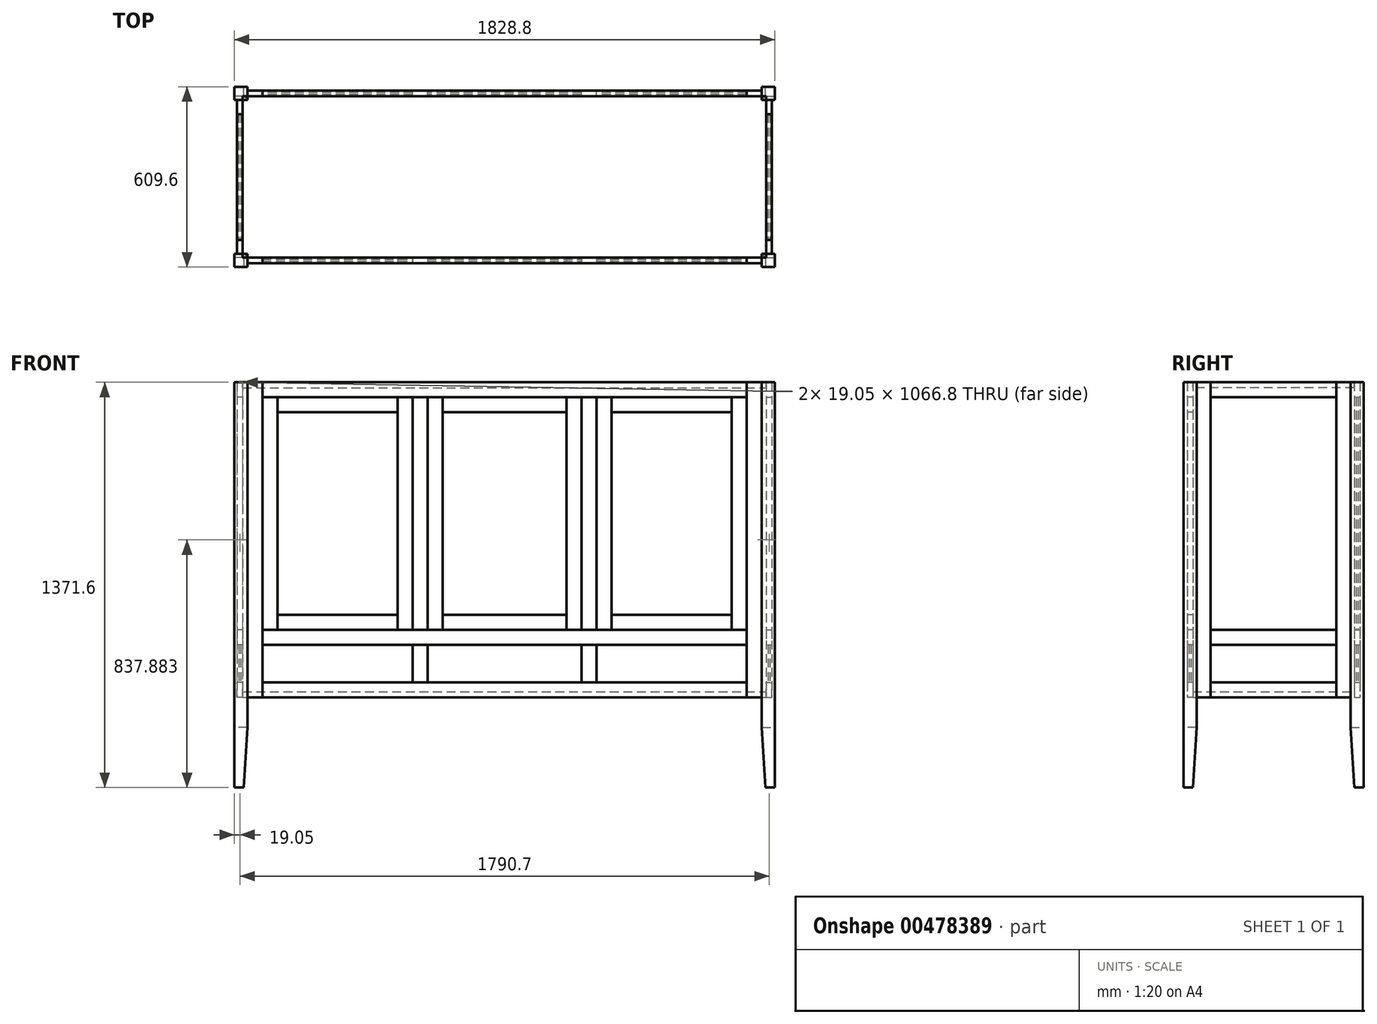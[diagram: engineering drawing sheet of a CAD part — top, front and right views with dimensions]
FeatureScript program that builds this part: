
annotation { "Feature Type Name" : "Feature", "Feature Type Description" : "" }
export const myFeature = defineFeature(function(context is Context, id is Id, definition is map)
    precondition{}
    {
        {
            var Q0;
            Q0=qCreatedBy(makeId("Front.planeOp"),FACE);
            var sketch = newSketch(context, id + "F0", { "sketchPlane" : qUnion([Q0])});
            skLineSegment(sketch, "E0.bottom", {"start": v(-628.95, 1371.6) * mm, "end": v(-584.5, 1371.6) * mm});
            skLineSegment(sketch, "E0.top", {"start": v(-628.95, 0) * mm, "end": v(-584.5, 0) * mm});
            skLineSegment(sketch, "E0.left", {"start": v(-628.95, 1371.6) * mm, "end": v(-628.95, 0) * mm});
            skLineSegment(sketch, "E0.right", {"start": v(-584.5, 1371.6) * mm, "end": v(-584.5, 0) * mm});
            skSolve(sketch);
        }
        {
            var Q0;
            Q0 = qSketchRegion(id + "F0", true);
            extrude(context, id + "F1", {"entities" : qUnion([Q0]), "depth" : 44.45 * mm});
        }
        {
            var Q0;
            Q0=makeQuery(id+"F1.opExtrude","CAP_FACE",FACE,{"disambiguationData":[OSD([sQuery(id+"F0.wireOp",EDGE,"E0.bottom"),sQuery(id+"F0.wireOp",EDGE,"E0.top"),sQuery(id+"F0.wireOp",EDGE,"E0.left"),sQuery(id+"F0.wireOp",EDGE,"E0.right")])],"isStart":false});
            var sketch = newSketch(context, id + "F2", { "sketchPlane" : qUnion([Q0])});
            skPoint(sketch, "E1", {"position": v(-584.5, 203.2) * mm});
            skPoint(sketch, "E2", {"position": v(-597.2, 0) * mm});
            skLineSegment(sketch, "E3", {"start": v(-597.2, 0) * mm, "end": v(-584.5, 203.2) * mm});
            skLineSegment(sketch, "E4", {"start": v(-597.2, 0) * mm, "end": v(-584.5, 0) * mm});
            skLineSegment(sketch, "E5", {"start": v(-584.5, 0) * mm, "end": v(-584.5, 203.2) * mm});
            skSolve(sketch);
        }
        {
            var Q0;
            Q0=makeQuery(id+"F2.imprint","IMPRINT",FACE,{"disambiguationData":[TD([[makeQuery(id+"F2.imprint","IMPRINT",EDGE,{"derivedFrom":sQuery(id+"F2.wireOp",EDGE,"E3")}),-1.0]])]});
            extrude(context, id + "F3", {"entities" : qUnion([Q0]), "operationType" : NewBodyOperationType.REMOVE, "endBound" : BoundingType.THROUGH_ALL, "oppositeDirection" : true, "depth" : 25.4 * mm});
        }
        {
            var Q0;
            Q0=makeQuery(id+"F1.opExtrude","SWEPT_FACE",FACE,{"disambiguationData":[OSD([sQuery(id+"F0.wireOp",EDGE,"E0.left")])]});
            var sketch = newSketch(context, id + "F4", { "sketchPlane" : qUnion([Q0])});
            skPoint(sketch, "E6", {"position": v(0, 203.2) * mm});
            skPoint(sketch, "E7", {"position": v(12.7, 0) * mm});
            skLineSegment(sketch, "E8", {"start": v(0, 203.2) * mm, "end": v(12.7, 0) * mm});
            skLineSegment(sketch, "E9", {"start": v(0, 0) * mm, "end": v(0, 203.2) * mm});
            skSolve(sketch);
        }
        {
            var Q0;
            {var subQ0=sQuery(id+"F4.wireOp",EDGE,"E8");Q0=makeQuery(id+"F4.imprint","IMPRINT",FACE,{"disambiguationData":[TD([[makeQuery(id+"F4.imprint","IMPRINT",EDGE,{"derivedFrom":subQ0}),-1.0]])]});}
            extrude(context, id + "F5", {"entities" : qUnion([Q0]), "operationType" : NewBodyOperationType.REMOVE, "endBound" : BoundingType.THROUGH_ALL, "oppositeDirection" : true, "depth" : 25.4 * mm});
        }
        {
            var Q0;
            Q0=makeQuery(id+"F1.opExtrude","CAP_FACE",FACE,{"disambiguationData":[OSD([sQuery(id+"F0.wireOp",EDGE,"E0.bottom"),sQuery(id+"F0.wireOp",EDGE,"E0.top"),sQuery(id+"F0.wireOp",EDGE,"E0.left"),sQuery(id+"F0.wireOp",EDGE,"E0.right")])],"isStart":false});
            cPlane(context, id + "F6", {"entities" : qUnion([Q0]), "cplaneType" : CPlaneType.OFFSET, "offset" : 304.8 * mm, "oppositeDirection" : true, "width" : 152.4 * mm, "height" : 152.4 * mm});
        }
        {
            var Q0;
            Q0=makeQuery(id+"F1.opExtrude","SWEPT_FACE",FACE,{"disambiguationData":[OSD([sQuery(id+"F0.wireOp",EDGE,"E0.left")])]});
            cPlane(context, id + "F7", {"entities" : qUnion([Q0]), "cplaneType" : CPlaneType.OFFSET, "offset" : 9.52 * mm, "oppositeDirection" : true, "width" : 152.4 * mm, "height" : 152.4 * mm});
        }
        {
            var Q0;
            Q0=qCreatedBy(id+"F7.planeOp",FACE);
            var sketch = newSketch(context, id + "F8", { "sketchPlane" : qUnion([Q0])});
            skPoint(sketch, "E10", {"position": v(0, 1371.28) * mm});
            skPoint(sketch, "E11", {"position": v(0, 304.48) * mm});
            skLineSegment(sketch, "E12.bottom", {"start": v(0, 1371.28) * mm, "end": v(-47.62, 1371.28) * mm});
            skLineSegment(sketch, "E12.top", {"start": v(0, 304.48) * mm, "end": v(-47.62, 304.48) * mm});
            skLineSegment(sketch, "E12.left", {"start": v(0, 1371.28) * mm, "end": v(0, 304.48) * mm});
            skLineSegment(sketch, "E12.right", {"start": v(-47.62, 1371.28) * mm, "end": v(-47.62, 304.48) * mm});
            skSolve(sketch);
        }
        {
            var Q0;
            Q0=makeQuery(id+"F8.imprint","IMPRINT",FACE,{"disambiguationData":[TD([[makeQuery(id+"F8.imprint","IMPRINT",EDGE,{"derivedFrom":sQuery(id+"F8.wireOp",EDGE,"E12.bottom")}),1.0]])]});
            extrude(context, id + "F9", {"entities" : qUnion([Q0]), "operationType" : NewBodyOperationType.ADD, "oppositeDirection" : true, "depth" : 19.05 * mm});
        }
        {
            var Q0;
            Q0=makeQuery(id+"F1.opExtrude","SWEPT_BODY",BODY,{"disambiguationData":[OSD([sQuery(id+"F0.wireOp",EDGE,"E0.bottom"),sQuery(id+"F0.wireOp",EDGE,"E0.top"),sQuery(id+"F0.wireOp",EDGE,"E0.left"),sQuery(id+"F0.wireOp",EDGE,"E0.right")])]});
            var Q1;
            Q1=qCreatedBy(id+"F6.planeOp",FACE);
            mirror(context, id + "F10", {"entities" : qUnion([Q0]), "mirrorPlane" : qUnion([Q1])});
        }
        {
            var Q0;
            Q0=qCreatedBy(id+"F7.planeOp",FACE);
            var sketch = newSketch(context, id + "F11", { "sketchPlane" : qUnion([Q0])});
            skLineSegment(sketch, "E13.bottom", {"start": v(-473.08, 1371.28) * mm, "end": v(-47.62, 1371.28) * mm});
            skLineSegment(sketch, "E13.top", {"start": v(-473.08, 1320.48) * mm, "end": v(-47.62, 1320.48) * mm});
            skLineSegment(sketch, "E13.left", {"start": v(-473.08, 1371.28) * mm, "end": v(-473.08, 1320.48) * mm});
            skLineSegment(sketch, "E13.right", {"start": v(-47.62, 1371.28) * mm, "end": v(-47.62, 1320.48) * mm});
            skSolve(sketch);
        }
        {
            var Q0;
            Q0=makeQuery(id+"F11.imprint","IMPRINT",FACE,{"disambiguationData":[TD([[makeQuery(id+"F11.imprint","IMPRINT",EDGE,{"derivedFrom":sQuery(id+"F11.wireOp",EDGE,"E13.bottom")}),-1.0]])]});
            extrude(context, id + "F12", {"entities" : qUnion([Q0]), "oppositeDirection" : true, "depth" : 19.05 * mm});
        }
        {
            var Q0;
            Q0=qCreatedBy(id+"F7.planeOp",FACE);
            var sketch = newSketch(context, id + "F13", { "sketchPlane" : qUnion([Q0])});
            skLineSegment(sketch, "E14.bottom", {"start": v(-473.08, 304.48) * mm, "end": v(-47.62, 304.48) * mm});
            skLineSegment(sketch, "E14.top", {"start": v(-473.08, 355.28) * mm, "end": v(-47.62, 355.28) * mm});
            skLineSegment(sketch, "E14.left", {"start": v(-473.08, 304.48) * mm, "end": v(-473.08, 355.28) * mm});
            skLineSegment(sketch, "E14.right", {"start": v(-47.62, 304.48) * mm, "end": v(-47.62, 355.28) * mm});
            skSolve(sketch);
        }
        {
            var Q0;
            Q0=makeQuery(id+"F13.imprint","IMPRINT",FACE,{"disambiguationData":[TD([[makeQuery(id+"F13.imprint","IMPRINT",EDGE,{"derivedFrom":sQuery(id+"F13.wireOp",EDGE,"E14.bottom")}),1.0]])]});
            extrude(context, id + "F14", {"entities" : qUnion([Q0]), "oppositeDirection" : true, "depth" : 19.05 * mm});
        }
        {
            var Q0;
            Q0=qCreatedBy(id+"F7.planeOp",FACE);
            var sketch = newSketch(context, id + "F15", { "sketchPlane" : qUnion([Q0])});
            skPoint(sketch, "E15", {"position": v(-473.08, 1371.28) * mm});
            skPoint(sketch, "E16", {"position": v(-473.08, 533.08) * mm});
            skLineSegment(sketch, "E17.bottom", {"start": v(-473.08, 533.08) * mm, "end": v(-47.62, 533.08) * mm});
            skLineSegment(sketch, "E17.top", {"start": v(-473.08, 482.28) * mm, "end": v(-47.62, 482.28) * mm});
            skLineSegment(sketch, "E17.left", {"start": v(-473.08, 533.08) * mm, "end": v(-473.08, 482.28) * mm});
            skLineSegment(sketch, "E17.right", {"start": v(-47.62, 533.08) * mm, "end": v(-47.62, 482.28) * mm});
            skSolve(sketch);
        }
        {
            var Q0;
            Q0=makeQuery(id+"F15.imprint","IMPRINT",FACE,{"disambiguationData":[TD([[makeQuery(id+"F15.imprint","IMPRINT",EDGE,{"derivedFrom":sQuery(id+"F15.wireOp",EDGE,"E17.bottom")}),-1.0]])]});
            extrude(context, id + "F16", {"entities" : qUnion([Q0]), "oppositeDirection" : true, "depth" : 19.05 * mm});
        }
        {
            var Q0;
            Q0=makeQuery(id+"F16.opExtrude","CAP_FACE",FACE,{"disambiguationData":[OSD([sQuery(id+"F15.wireOp",EDGE,"E17.bottom"),sQuery(id+"F15.wireOp",EDGE,"E17.top"),sQuery(id+"F15.wireOp",EDGE,"E17.left"),sQuery(id+"F15.wireOp",EDGE,"E17.right")])],"isStart":true});
            cPlane(context, id + "F17", {"entities" : qUnion([Q0]), "cplaneType" : CPlaneType.OFFSET, "offset" : 6.35 * mm, "oppositeDirection" : true, "width" : 152.4 * mm, "height" : 152.4 * mm});
        }
        {
            var Q0;
            Q0=qCreatedBy(id+"F17.planeOp",FACE);
            var sketch = newSketch(context, id + "F18", { "sketchPlane" : qUnion([Q0])});
            skLineSegment(sketch, "E18.bottom", {"start": v(-473.08, 482.28) * mm, "end": v(-47.62, 482.28) * mm});
            skLineSegment(sketch, "E18.top", {"start": v(-473.08, 355.28) * mm, "end": v(-47.62, 355.28) * mm});
            skLineSegment(sketch, "E18.left", {"start": v(-473.08, 482.28) * mm, "end": v(-473.08, 355.28) * mm});
            skLineSegment(sketch, "E18.right", {"start": v(-47.62, 482.28) * mm, "end": v(-47.62, 355.28) * mm});
            skSolve(sketch);
        }
        {
            var Q0;
            Q0=makeQuery(id+"F18.imprint","IMPRINT",FACE,{"disambiguationData":[TD([[makeQuery(id+"F18.imprint","IMPRINT",EDGE,{"derivedFrom":sQuery(id+"F18.wireOp",EDGE,"E18.bottom")}),-1.0]])]});
            extrude(context, id + "F19", {"entities" : qUnion([Q0]), "oppositeDirection" : true, "depth" : 6.35 * mm});
        }
        {
            var Q0;
            Q0=makeQuery(id+"F1.opExtrude","SWEPT_FACE",FACE,{"disambiguationData":[OSD([sQuery(id+"F0.wireOp",EDGE,"E0.left")])]});
            cPlane(context, id + "F20", {"entities" : qUnion([Q0]), "cplaneType" : CPlaneType.OFFSET, "offset" : 914.4 * mm, "oppositeDirection" : true, "width" : 152.4 * mm, "height" : 152.4 * mm});
        }
        {
            var Q0;
            Q0=makeQuery(id+"F1.opExtrude","SWEPT_BODY",BODY,{"disambiguationData":[OSD([sQuery(id+"F0.wireOp",EDGE,"E0.bottom"),sQuery(id+"F0.wireOp",EDGE,"E0.top"),sQuery(id+"F0.wireOp",EDGE,"E0.left"),sQuery(id+"F0.wireOp",EDGE,"E0.right")])]});
            var Q1;
            Q1=makeQuery(id+"F14.opExtrude","SWEPT_BODY",BODY,{"disambiguationData":[OSD([sQuery(id+"F13.wireOp",EDGE,"E14.bottom"),sQuery(id+"F13.wireOp",EDGE,"E14.top"),sQuery(id+"F13.wireOp",EDGE,"E14.left"),sQuery(id+"F13.wireOp",EDGE,"E14.right")])]});
            var Q2;
            Q2=makeQuery(id+"F12.opExtrude","SWEPT_BODY",BODY,{"disambiguationData":[OSD([sQuery(id+"F11.wireOp",EDGE,"E13.bottom"),sQuery(id+"F11.wireOp",EDGE,"E13.top"),sQuery(id+"F11.wireOp",EDGE,"E13.left"),sQuery(id+"F11.wireOp",EDGE,"E13.right")])]});
            var Q3;
            Q3=makeQuery(id+"F10.opPattern","COPY",BODY,{"derivedFrom":makeQuery(id+"F1.opExtrude","SWEPT_BODY",BODY,{"disambiguationData":[OSD([sQuery(id+"F0.wireOp",EDGE,"E0.bottom"),sQuery(id+"F0.wireOp",EDGE,"E0.top"),sQuery(id+"F0.wireOp",EDGE,"E0.left"),sQuery(id+"F0.wireOp",EDGE,"E0.right")])]}),"instanceName":"1"});
            var Q4;
            Q4=makeQuery(id+"F16.opExtrude","SWEPT_BODY",BODY,{"disambiguationData":[OSD([sQuery(id+"F15.wireOp",EDGE,"E17.bottom"),sQuery(id+"F15.wireOp",EDGE,"E17.top"),sQuery(id+"F15.wireOp",EDGE,"E17.left"),sQuery(id+"F15.wireOp",EDGE,"E17.right")])]});
            var Q5;
            Q5=makeQuery(id+"F19.opExtrude","SWEPT_BODY",BODY,{"disambiguationData":[OSD([sQuery(id+"F18.wireOp",EDGE,"E18.bottom"),sQuery(id+"F18.wireOp",EDGE,"E18.top"),sQuery(id+"F18.wireOp",EDGE,"E18.left"),sQuery(id+"F18.wireOp",EDGE,"E18.right")])]});
            var Q6;
            Q6=qCreatedBy(id+"F20.planeOp",FACE);
            mirror(context, id + "F21", {"entities" : qUnion([Q0, Q1, Q2, Q3, Q4, Q5]), "mirrorPlane" : qUnion([Q6])});
        }
        {
            var Q0;
            Q0=makeQuery(id+"F21.opPattern","COPY",FACE,{"derivedFrom":makeQuery(id+"F1.opExtrude","CAP_FACE",FACE,{"disambiguationData":[OSD([sQuery(id+"F0.wireOp",EDGE,"E0.bottom"),sQuery(id+"F0.wireOp",EDGE,"E0.top"),sQuery(id+"F0.wireOp",EDGE,"E0.left"),sQuery(id+"F0.wireOp",EDGE,"E0.right")])],"isStart":false}),"instanceName":"1"});
            cPlane(context, id + "F22", {"entities" : qUnion([Q0]), "cplaneType" : CPlaneType.OFFSET, "offset" : 12.7 * mm, "oppositeDirection" : true, "width" : 152.4 * mm, "height" : 152.4 * mm});
        }
        {
            var Q0;
            Q0=qCreatedBy(id+"F22.planeOp",FACE);
            var sketch = newSketch(context, id + "F23", { "sketchPlane" : qUnion([Q0])});
            skLineSegment(sketch, "E19.bottom", {"start": v(-584.5, 1371.6) * mm, "end": v(-533.7, 1371.6) * mm});
            skLineSegment(sketch, "E19.top", {"start": v(-584.5, 304.48) * mm, "end": v(-533.7, 304.48) * mm});
            skLineSegment(sketch, "E19.left", {"start": v(-584.5, 1371.6) * mm, "end": v(-584.5, 304.48) * mm});
            skLineSegment(sketch, "E19.right", {"start": v(-533.7, 1371.6) * mm, "end": v(-533.7, 304.48) * mm});
            skSolve(sketch);
        }
        {
            var Q0;
            Q0 = qSketchRegion(id + "F23", true);
            extrude(context, id + "F24", {"entities" : qUnion([Q0]), "oppositeDirection" : true, "depth" : 19.05 * mm});
        }
        {
            var Q0;
            Q0=qCreatedBy(id+"F22.planeOp",FACE);
            var sketch = newSketch(context, id + "F25", { "sketchPlane" : qUnion([Q0])});
            skLineSegment(sketch, "E20.bottom", {"start": v(-533.7, 1371.6) * mm, "end": v(1104.6, 1371.6) * mm});
            skLineSegment(sketch, "E20.top", {"start": v(-533.7, 1320.8) * mm, "end": v(1104.6, 1320.8) * mm});
            skLineSegment(sketch, "E20.left", {"start": v(-533.7, 1371.6) * mm, "end": v(-533.7, 1320.8) * mm});
            skLineSegment(sketch, "E20.right", {"start": v(1104.6, 1371.6) * mm, "end": v(1104.6, 1320.8) * mm});
            skSolve(sketch);
        }
        {
            var Q0;
            Q0 = qSketchRegion(id + "F25", true);
            extrude(context, id + "F26", {"entities" : qUnion([Q0]), "oppositeDirection" : true, "depth" : 19.05 * mm});
        }
        {
            var Q0;
            Q0=makeQuery(id+"F24.opExtrude","SWEPT_BODY",BODY,{"disambiguationData":[OSD([sQuery(id+"F23.wireOp",EDGE,"E19.bottom"),sQuery(id+"F23.wireOp",EDGE,"E19.top"),sQuery(id+"F23.wireOp",EDGE,"E19.left"),sQuery(id+"F23.wireOp",EDGE,"E19.right")])]});
            var Q1;
            Q1=qCreatedBy(id+"F20.planeOp",FACE);
            mirror(context, id + "F27", {"entities" : qUnion([Q0]), "mirrorPlane" : qUnion([Q1])});
        }
        {
            var Q0;
            Q0=qCreatedBy(id+"F22.planeOp",FACE);
            var sketch = newSketch(context, id + "F28", { "sketchPlane" : qUnion([Q0])});
            skLineSegment(sketch, "E21.bottom", {"start": v(-533.7, 355.28) * mm, "end": v(1104.6, 355.28) * mm});
            skLineSegment(sketch, "E21.top", {"start": v(-533.7, 304.48) * mm, "end": v(1104.6, 304.48) * mm});
            skLineSegment(sketch, "E21.left", {"start": v(-533.7, 355.28) * mm, "end": v(-533.7, 304.48) * mm});
            skLineSegment(sketch, "E21.right", {"start": v(1104.6, 355.28) * mm, "end": v(1104.6, 304.48) * mm});
            skSolve(sketch);
        }
        {
            var Q0;
            Q0 = qSketchRegion(id + "F28", true);
            extrude(context, id + "F29", {"entities" : qUnion([Q0]), "oppositeDirection" : true, "depth" : 19.05 * mm});
        }
        {
            var Q0;
            Q0=qCreatedBy(id+"F22.planeOp",FACE);
            var sketch = newSketch(context, id + "F30", { "sketchPlane" : qUnion([Q0])});
            skLineSegment(sketch, "E22.bottom", {"start": v(-533.7, 533.08) * mm, "end": v(1104.6, 533.08) * mm});
            skLineSegment(sketch, "E22.top", {"start": v(-533.7, 482.28) * mm, "end": v(1104.6, 482.28) * mm});
            skLineSegment(sketch, "E22.left", {"start": v(-533.7, 533.08) * mm, "end": v(-533.7, 482.28) * mm});
            skLineSegment(sketch, "E22.right", {"start": v(1104.6, 533.08) * mm, "end": v(1104.6, 482.28) * mm});
            skSolve(sketch);
        }
        {
            var Q0;
            Q0 = qSketchRegion(id + "F30", true);
            extrude(context, id + "F31", {"entities" : qUnion([Q0]), "oppositeDirection" : true, "depth" : 19.05 * mm});
        }
        {
            var Q0;
            Q0=qCreatedBy(id+"F22.planeOp",FACE);
            var sketch = newSketch(context, id + "F32", { "sketchPlane" : qUnion([Q0])});
            skLineSegment(sketch, "E23.bottom", {"start": v(-25.7, 1320.8) * mm, "end": v(25.1, 1320.8) * mm});
            skLineSegment(sketch, "E23.top", {"start": v(-25.7, 533.08) * mm, "end": v(25.1, 533.08) * mm});
            skLineSegment(sketch, "E23.left", {"start": v(-25.7, 1320.8) * mm, "end": v(-25.7, 533.08) * mm});
            skLineSegment(sketch, "E23.right", {"start": v(25.1, 1320.8) * mm, "end": v(25.1, 533.08) * mm});
            skSolve(sketch);
        }
        {
            var Q0;
            Q0 = qSketchRegion(id + "F32", true);
            extrude(context, id + "F33", {"entities" : qUnion([Q0]), "oppositeDirection" : true, "depth" : 19.05 * mm});
        }
        {
            var Q0;
            Q0=qCreatedBy(id+"F22.planeOp",FACE);
            var sketch = newSketch(context, id + "F34", { "sketchPlane" : qUnion([Q0])});
            skLineSegment(sketch, "E24.bottom", {"start": v(-25.7, 482.28) * mm, "end": v(25.1, 482.28) * mm});
            skLineSegment(sketch, "E24.top", {"start": v(-25.7, 355.28) * mm, "end": v(25.1, 355.28) * mm});
            skLineSegment(sketch, "E24.left", {"start": v(-25.7, 482.28) * mm, "end": v(-25.7, 355.28) * mm});
            skLineSegment(sketch, "E24.right", {"start": v(25.1, 482.28) * mm, "end": v(25.1, 355.28) * mm});
            skSolve(sketch);
        }
        {
            var Q0;
            Q0 = qSketchRegion(id + "F34", true);
            extrude(context, id + "F35", {"entities" : qUnion([Q0]), "oppositeDirection" : true, "depth" : 19.05 * mm});
        }
        {
            var Q0;
            Q0=makeQuery(id+"F33.opExtrude","SWEPT_BODY",BODY,{"disambiguationData":[OSD([sQuery(id+"F32.wireOp",EDGE,"E23.bottom"),sQuery(id+"F32.wireOp",EDGE,"E23.top"),sQuery(id+"F32.wireOp",EDGE,"E23.left"),sQuery(id+"F32.wireOp",EDGE,"E23.right")])]});
            var Q1;
            Q1=makeQuery(id+"F35.opExtrude","SWEPT_BODY",BODY,{"disambiguationData":[OSD([sQuery(id+"F34.wireOp",EDGE,"E24.bottom"),sQuery(id+"F34.wireOp",EDGE,"E24.top"),sQuery(id+"F34.wireOp",EDGE,"E24.left"),sQuery(id+"F34.wireOp",EDGE,"E24.right")])]});
            var Q2;
            Q2=qCreatedBy(id+"F20.planeOp",FACE);
            mirror(context, id + "F36", {"entities" : qUnion([Q0, Q1]), "mirrorPlane" : qUnion([Q2])});
        }
        {
            var Q0;
            Q0=makeQuery(id+"F31.opExtrude","CAP_FACE",FACE,{"disambiguationData":[OSD([sQuery(id+"F30.wireOp",EDGE,"E22.bottom"),sQuery(id+"F30.wireOp",EDGE,"E22.top"),sQuery(id+"F30.wireOp",EDGE,"E22.left"),sQuery(id+"F30.wireOp",EDGE,"E22.right")])],"isStart":true});
            cPlane(context, id + "F37", {"entities" : qUnion([Q0]), "cplaneType" : CPlaneType.OFFSET, "offset" : 6.35 * mm, "oppositeDirection" : true, "width" : 152.4 * mm, "height" : 152.4 * mm});
        }
        {
            var Q0;
            Q0=qCreatedBy(id+"F37.planeOp",FACE);
            var sketch = newSketch(context, id + "F38", { "sketchPlane" : qUnion([Q0])});
            skLineSegment(sketch, "E25.bottom", {"start": v(-533.7, 482.28) * mm, "end": v(-25.7, 482.28) * mm});
            skLineSegment(sketch, "E25.top", {"start": v(-533.7, 355.28) * mm, "end": v(-25.7, 355.28) * mm});
            skLineSegment(sketch, "E25.left", {"start": v(-533.7, 482.28) * mm, "end": v(-533.7, 355.28) * mm});
            skLineSegment(sketch, "E25.right", {"start": v(-25.7, 482.28) * mm, "end": v(-25.7, 355.28) * mm});
            skLineSegment(sketch, "E26.bottom", {"start": v(25.1, 482.28) * mm, "end": v(545.8, 482.28) * mm});
            skLineSegment(sketch, "E26.top", {"start": v(25.1, 355.28) * mm, "end": v(545.8, 355.28) * mm});
            skLineSegment(sketch, "E26.left", {"start": v(25.1, 482.28) * mm, "end": v(25.1, 355.28) * mm});
            skLineSegment(sketch, "E26.right", {"start": v(545.8, 482.28) * mm, "end": v(545.8, 355.28) * mm});
            skLineSegment(sketch, "E27.bottom", {"start": v(596.6, 482.28) * mm, "end": v(1104.6, 482.28) * mm});
            skLineSegment(sketch, "E27.top", {"start": v(596.6, 355.28) * mm, "end": v(1104.6, 355.28) * mm});
            skLineSegment(sketch, "E27.left", {"start": v(596.6, 482.28) * mm, "end": v(596.6, 355.28) * mm});
            skLineSegment(sketch, "E27.right", {"start": v(1104.6, 482.28) * mm, "end": v(1104.6, 355.28) * mm});
            skSolve(sketch);
        }
        {
            var Q0;
            Q0 = qSketchRegion(id + "F38", true);
            extrude(context, id + "F39", {"entities" : qUnion([Q0]), "oppositeDirection" : true, "depth" : 6.35 * mm});
        }
        {
            var Q0;
            Q0=makeQuery(id+"F24.opExtrude","SWEPT_BODY",BODY,{"disambiguationData":[OSD([sQuery(id+"F23.wireOp",EDGE,"E19.bottom"),sQuery(id+"F23.wireOp",EDGE,"E19.top"),sQuery(id+"F23.wireOp",EDGE,"E19.left"),sQuery(id+"F23.wireOp",EDGE,"E19.right")])]});
            var Q1;
            Q1=makeQuery(id+"F26.opExtrude","SWEPT_BODY",BODY,{"disambiguationData":[OSD([sQuery(id+"F25.wireOp",EDGE,"E20.bottom"),sQuery(id+"F25.wireOp",EDGE,"E20.top"),sQuery(id+"F25.wireOp",EDGE,"E20.left"),sQuery(id+"F25.wireOp",EDGE,"E20.right")])]});
            var Q2;
            Q2=makeQuery(id+"F33.opExtrude","SWEPT_BODY",BODY,{"disambiguationData":[OSD([sQuery(id+"F32.wireOp",EDGE,"E23.bottom"),sQuery(id+"F32.wireOp",EDGE,"E23.top"),sQuery(id+"F32.wireOp",EDGE,"E23.left"),sQuery(id+"F32.wireOp",EDGE,"E23.right")])]});
            var Q3;
            Q3=makeQuery(id+"F36.opPattern","COPY",BODY,{"derivedFrom":makeQuery(id+"F33.opExtrude","SWEPT_BODY",BODY,{"disambiguationData":[OSD([sQuery(id+"F32.wireOp",EDGE,"E23.bottom"),sQuery(id+"F32.wireOp",EDGE,"E23.top"),sQuery(id+"F32.wireOp",EDGE,"E23.left"),sQuery(id+"F32.wireOp",EDGE,"E23.right")])]}),"instanceName":"1"});
            var Q4;
            Q4=makeQuery(id+"F27.opPattern","COPY",BODY,{"derivedFrom":makeQuery(id+"F24.opExtrude","SWEPT_BODY",BODY,{"disambiguationData":[OSD([sQuery(id+"F23.wireOp",EDGE,"E19.bottom"),sQuery(id+"F23.wireOp",EDGE,"E19.top"),sQuery(id+"F23.wireOp",EDGE,"E19.left"),sQuery(id+"F23.wireOp",EDGE,"E19.right")])]}),"instanceName":"1"});
            var Q5;
            Q5=makeQuery(id+"F31.opExtrude","SWEPT_BODY",BODY,{"disambiguationData":[OSD([sQuery(id+"F30.wireOp",EDGE,"E22.bottom"),sQuery(id+"F30.wireOp",EDGE,"E22.top"),sQuery(id+"F30.wireOp",EDGE,"E22.left"),sQuery(id+"F30.wireOp",EDGE,"E22.right")])]});
            var Q6;
            Q6=makeQuery(id+"F29.opExtrude","SWEPT_BODY",BODY,{"disambiguationData":[OSD([sQuery(id+"F28.wireOp",EDGE,"E21.bottom"),sQuery(id+"F28.wireOp",EDGE,"E21.top"),sQuery(id+"F28.wireOp",EDGE,"E21.left"),sQuery(id+"F28.wireOp",EDGE,"E21.right")])]});
            var Q7;
            Q7=makeQuery(id+"F36.opPattern","COPY",BODY,{"derivedFrom":makeQuery(id+"F35.opExtrude","SWEPT_BODY",BODY,{"disambiguationData":[OSD([sQuery(id+"F34.wireOp",EDGE,"E24.bottom"),sQuery(id+"F34.wireOp",EDGE,"E24.top"),sQuery(id+"F34.wireOp",EDGE,"E24.left"),sQuery(id+"F34.wireOp",EDGE,"E24.right")])]}),"instanceName":"1"});
            var Q8;
            Q8=makeQuery(id+"F35.opExtrude","SWEPT_BODY",BODY,{"disambiguationData":[OSD([sQuery(id+"F34.wireOp",EDGE,"E24.bottom"),sQuery(id+"F34.wireOp",EDGE,"E24.top"),sQuery(id+"F34.wireOp",EDGE,"E24.left"),sQuery(id+"F34.wireOp",EDGE,"E24.right")])]});
            var Q9;
            Q9=makeQuery(id+"F39.opExtrude","SWEPT_BODY",BODY,{"disambiguationData":[OSD([sQuery(id+"F38.wireOp",EDGE,"E25.bottom"),sQuery(id+"F38.wireOp",EDGE,"E25.top"),sQuery(id+"F38.wireOp",EDGE,"E25.left"),sQuery(id+"F38.wireOp",EDGE,"E25.right")])]});
            var Q10;
            Q10=makeQuery(id+"F39.opExtrude","SWEPT_BODY",BODY,{"disambiguationData":[OSD([sQuery(id+"F38.wireOp",EDGE,"E26.bottom"),sQuery(id+"F38.wireOp",EDGE,"E26.top"),sQuery(id+"F38.wireOp",EDGE,"E26.left"),sQuery(id+"F38.wireOp",EDGE,"E26.right")])]});
            var Q11;
            Q11=makeQuery(id+"F39.opExtrude","SWEPT_BODY",BODY,{"disambiguationData":[OSD([sQuery(id+"F38.wireOp",EDGE,"E27.bottom"),sQuery(id+"F38.wireOp",EDGE,"E27.top"),sQuery(id+"F38.wireOp",EDGE,"E27.left"),sQuery(id+"F38.wireOp",EDGE,"E27.right")])]});
            var Q12;
            Q12=qCreatedBy(id+"F6.planeOp",FACE);
            mirror(context, id + "F40", {"entities" : qUnion([Q0, Q1, Q2, Q3, Q4, Q5, Q6, Q7, Q8, Q9, Q10, Q11]), "mirrorPlane" : qUnion([Q12])});
        }
        {
            var Q0;
            Q0=qCreatedBy(id+"F22.planeOp",FACE);
            var sketch = newSketch(context, id + "F41", { "sketchPlane" : qUnion([Q0])});
            skLineSegment(sketch, "E28.bottom", {"start": v(-533.7, 1320.8) * mm, "end": v(-482.9, 1320.8) * mm});
            skLineSegment(sketch, "E28.top", {"start": v(-533.7, 533.08) * mm, "end": v(-482.9, 533.08) * mm});
            skLineSegment(sketch, "E28.left", {"start": v(-533.7, 1320.8) * mm, "end": v(-533.7, 533.08) * mm});
            skLineSegment(sketch, "E28.right", {"start": v(-482.9, 1320.8) * mm, "end": v(-482.9, 533.08) * mm});
            skSolve(sketch);
        }
        {
            var Q0;
            Q0 = qSketchRegion(id + "F41", true);
            extrude(context, id + "F42", {"entities" : qUnion([Q0]), "oppositeDirection" : true, "depth" : 19.05 * mm});
        }
        {
            var Q0;
            Q0=qCreatedBy(id+"F22.planeOp",FACE);
            var sketch = newSketch(context, id + "F43", { "sketchPlane" : qUnion([Q0])});
            skLineSegment(sketch, "E29.bottom", {"start": v(-76.5, 1320.8) * mm, "end": v(-25.7, 1320.8) * mm});
            skLineSegment(sketch, "E29.top", {"start": v(-76.5, 533.08) * mm, "end": v(-25.7, 533.08) * mm});
            skLineSegment(sketch, "E29.left", {"start": v(-76.5, 1320.8) * mm, "end": v(-76.5, 533.08) * mm});
            skLineSegment(sketch, "E29.right", {"start": v(-25.7, 1320.8) * mm, "end": v(-25.7, 533.08) * mm});
            skSolve(sketch);
        }
        {
            var Q0;
            Q0 = qSketchRegion(id + "F43", true);
            extrude(context, id + "F44", {"entities" : qUnion([Q0]), "oppositeDirection" : true, "depth" : 19.05 * mm});
        }
        {
            var Q0;
            Q0=qCreatedBy(id+"F22.planeOp",FACE);
            var sketch = newSketch(context, id + "F45", { "sketchPlane" : qUnion([Q0])});
            skLineSegment(sketch, "E30.bottom", {"start": v(-482.9, 1320.8) * mm, "end": v(-76.5, 1320.8) * mm});
            skLineSegment(sketch, "E30.top", {"start": v(-482.9, 1270) * mm, "end": v(-76.5, 1270) * mm});
            skLineSegment(sketch, "E30.left", {"start": v(-482.9, 1320.8) * mm, "end": v(-482.9, 1270) * mm});
            skLineSegment(sketch, "E30.right", {"start": v(-76.5, 1320.8) * mm, "end": v(-76.5, 1270) * mm});
            skSolve(sketch);
        }
        {
            var Q0;
            Q0 = qSketchRegion(id + "F45", true);
            extrude(context, id + "F46", {"entities" : qUnion([Q0]), "oppositeDirection" : true, "depth" : 19.05 * mm});
        }
        {
            var Q0;
            Q0=qCreatedBy(id+"F22.planeOp",FACE);
            var sketch = newSketch(context, id + "F47", { "sketchPlane" : qUnion([Q0])});
            skLineSegment(sketch, "E31.bottom", {"start": v(-482.9, 583.88) * mm, "end": v(-76.5, 583.88) * mm});
            skLineSegment(sketch, "E31.top", {"start": v(-482.9, 533.08) * mm, "end": v(-76.5, 533.08) * mm});
            skLineSegment(sketch, "E31.left", {"start": v(-482.9, 583.88) * mm, "end": v(-482.9, 533.08) * mm});
            skLineSegment(sketch, "E31.right", {"start": v(-76.5, 583.88) * mm, "end": v(-76.5, 533.08) * mm});
            skSolve(sketch);
        }
        {
            var Q0;
            Q0 = qSketchRegion(id + "F47", true);
            extrude(context, id + "F48", {"entities" : qUnion([Q0]), "oppositeDirection" : true, "depth" : 19.05 * mm});
        }
        {
            var Q0;
            Q0=makeQuery(id+"F42.opExtrude","SWEPT_BODY",BODY,{"disambiguationData":[OSD([sQuery(id+"F41.wireOp",EDGE,"E28.bottom"),sQuery(id+"F41.wireOp",EDGE,"E28.top"),sQuery(id+"F41.wireOp",EDGE,"E28.left"),sQuery(id+"F41.wireOp",EDGE,"E28.right")])]});
            var Q1;
            Q1=makeQuery(id+"F46.opExtrude","SWEPT_BODY",BODY,{"disambiguationData":[OSD([sQuery(id+"F45.wireOp",EDGE,"E30.bottom"),sQuery(id+"F45.wireOp",EDGE,"E30.top"),sQuery(id+"F45.wireOp",EDGE,"E30.left"),sQuery(id+"F45.wireOp",EDGE,"E30.right")])]});
            var Q2;
            Q2=makeQuery(id+"F44.opExtrude","SWEPT_BODY",BODY,{"disambiguationData":[OSD([sQuery(id+"F43.wireOp",EDGE,"E29.bottom"),sQuery(id+"F43.wireOp",EDGE,"E29.top"),sQuery(id+"F43.wireOp",EDGE,"E29.left"),sQuery(id+"F43.wireOp",EDGE,"E29.right")])]});
            var Q3;
            Q3=makeQuery(id+"F48.opExtrude","SWEPT_BODY",BODY,{"disambiguationData":[OSD([sQuery(id+"F47.wireOp",EDGE,"E31.bottom"),sQuery(id+"F47.wireOp",EDGE,"E31.top"),sQuery(id+"F47.wireOp",EDGE,"E31.left"),sQuery(id+"F47.wireOp",EDGE,"E31.right")])]});
            var Q4;
            Q4=qCreatedBy(id+"F20.planeOp",FACE);
            mirror(context, id + "F49", {"entities" : qUnion([Q0, Q1, Q2, Q3]), "mirrorPlane" : qUnion([Q4])});
        }
        {
            var Q0;
            Q0=qCreatedBy(id+"F22.planeOp",FACE);
            var sketch = newSketch(context, id + "F50", { "sketchPlane" : qUnion([Q0])});
            skLineSegment(sketch, "E32.bottom", {"start": v(25.1, 1320.8) * mm, "end": v(75.9, 1320.8) * mm});
            skLineSegment(sketch, "E32.top", {"start": v(25.1, 533.08) * mm, "end": v(75.9, 533.08) * mm});
            skLineSegment(sketch, "E32.left", {"start": v(25.1, 1320.8) * mm, "end": v(25.1, 533.08) * mm});
            skLineSegment(sketch, "E32.right", {"start": v(75.9, 1320.8) * mm, "end": v(75.9, 533.08) * mm});
            skSolve(sketch);
        }
        {
            var Q0;
            Q0 = qSketchRegion(id + "F50", true);
            extrude(context, id + "F51", {"entities" : qUnion([Q0]), "oppositeDirection" : true, "depth" : 19.05 * mm});
        }
        {
            var Q0;
            Q0=qCreatedBy(id+"F22.planeOp",FACE);
            var sketch = newSketch(context, id + "F52", { "sketchPlane" : qUnion([Q0])});
            skLineSegment(sketch, "E33.bottom", {"start": v(495, 1320.8) * mm, "end": v(545.8, 1320.8) * mm});
            skLineSegment(sketch, "E33.top", {"start": v(495, 533.08) * mm, "end": v(545.8, 533.08) * mm});
            skLineSegment(sketch, "E33.left", {"start": v(495, 1320.8) * mm, "end": v(495, 533.08) * mm});
            skLineSegment(sketch, "E33.right", {"start": v(545.8, 1320.8) * mm, "end": v(545.8, 533.08) * mm});
            skSolve(sketch);
        }
        {
            var Q0;
            Q0 = qSketchRegion(id + "F52", true);
            extrude(context, id + "F53", {"entities" : qUnion([Q0]), "oppositeDirection" : true, "depth" : 19.05 * mm});
        }
        {
            var Q0;
            Q0=qCreatedBy(id+"F22.planeOp",FACE);
            var sketch = newSketch(context, id + "F54", { "sketchPlane" : qUnion([Q0])});
            skLineSegment(sketch, "E34.bottom", {"start": v(75.9, 1320.8) * mm, "end": v(495, 1320.8) * mm});
            skLineSegment(sketch, "E34.top", {"start": v(75.9, 1270) * mm, "end": v(495, 1270) * mm});
            skLineSegment(sketch, "E34.left", {"start": v(75.9, 1320.8) * mm, "end": v(75.9, 1270) * mm});
            skLineSegment(sketch, "E34.right", {"start": v(495, 1320.8) * mm, "end": v(495, 1270) * mm});
            skSolve(sketch);
        }
        {
            var Q0;
            Q0 = qSketchRegion(id + "F54", true);
            extrude(context, id + "F55", {"entities" : qUnion([Q0]), "oppositeDirection" : true, "depth" : 19.05 * mm});
        }
        {
            var Q0;
            Q0=qCreatedBy(id+"F22.planeOp",FACE);
            var sketch = newSketch(context, id + "F56", { "sketchPlane" : qUnion([Q0])});
            skLineSegment(sketch, "E35.bottom", {"start": v(75.9, 583.88) * mm, "end": v(495, 583.88) * mm});
            skLineSegment(sketch, "E35.top", {"start": v(75.9, 533.08) * mm, "end": v(495, 533.08) * mm});
            skLineSegment(sketch, "E35.left", {"start": v(75.9, 583.88) * mm, "end": v(75.9, 533.08) * mm});
            skLineSegment(sketch, "E35.right", {"start": v(495, 583.88) * mm, "end": v(495, 533.08) * mm});
            skSolve(sketch);
        }
        {
            var Q0;
            Q0 = qSketchRegion(id + "F56", true);
            extrude(context, id + "F57", {"entities" : qUnion([Q0]), "oppositeDirection" : true, "depth" : 19.05 * mm});
        }
        {
            var Q0;
            Q0=makeQuery(id+"F40.opPattern","COPY",FACE,{"derivedFrom":makeQuery(id+"F39.opExtrude","CAP_FACE",FACE,{"disambiguationData":[OSD([sQuery(id+"F38.wireOp",EDGE,"E27.bottom"),sQuery(id+"F38.wireOp",EDGE,"E27.top"),sQuery(id+"F38.wireOp",EDGE,"E27.left"),sQuery(id+"F38.wireOp",EDGE,"E27.right")])],"isStart":true}),"instanceName":"1"});
            var sketch = newSketch(context, id + "F58", { "sketchPlane" : qUnion([Q0])});
            skLineSegment(sketch, "E36.bottom", {"start": v(-1104.6, 1320.8) * mm, "end": v(-596.6, 1320.8) * mm});
            skLineSegment(sketch, "E36.top", {"start": v(-1104.6, 533.08) * mm, "end": v(-596.6, 533.08) * mm});
            skLineSegment(sketch, "E36.left", {"start": v(-1104.6, 1320.8) * mm, "end": v(-1104.6, 533.08) * mm});
            skLineSegment(sketch, "E36.right", {"start": v(-596.6, 1320.8) * mm, "end": v(-596.6, 533.08) * mm});
            skLineSegment(sketch, "E37.bottom", {"start": v(-545.8, 1320.8) * mm, "end": v(-25.1, 1320.8) * mm});
            skLineSegment(sketch, "E37.top", {"start": v(-545.8, 533.08) * mm, "end": v(-25.1, 533.08) * mm});
            skLineSegment(sketch, "E37.left", {"start": v(-545.8, 1320.8) * mm, "end": v(-545.8, 533.08) * mm});
            skLineSegment(sketch, "E37.right", {"start": v(-25.1, 1320.8) * mm, "end": v(-25.1, 533.08) * mm});
            skLineSegment(sketch, "E38.bottom", {"start": v(25.7, 1320.8) * mm, "end": v(533.7, 1320.8) * mm});
            skLineSegment(sketch, "E38.top", {"start": v(25.7, 533.08) * mm, "end": v(533.7, 533.08) * mm});
            skLineSegment(sketch, "E38.left", {"start": v(25.7, 1320.8) * mm, "end": v(25.7, 533.08) * mm});
            skLineSegment(sketch, "E38.right", {"start": v(533.7, 1320.8) * mm, "end": v(533.7, 533.08) * mm});
            skSolve(sketch);
        }
        {
            var Q0;
            Q0 = qSketchRegion(id + "F58", true);
            extrude(context, id + "F59", {"entities" : qUnion([Q0]), "oppositeDirection" : true, "depth" : 6.35 * mm});
        }
        {
            var Q0;
            Q0=makeQuery(id+"F10.opPattern","COPY",FACE,{"derivedFrom":makeQuery(id+"F1.opExtrude","SWEPT_FACE",FACE,{"disambiguationData":[OSD([sQuery(id+"F0.wireOp",EDGE,"E0.bottom")])]}),"instanceName":"1"});
            var sketch = newSketch(context, id + "F60", { "sketchPlane" : qUnion([Q0])});
            skLineSegment(sketch, "E39.bottom", {"start": v(-600.37, 533.4) * mm, "end": v(1171.28, 533.4) * mm});
            skLineSegment(sketch, "E39.top", {"start": v(-600.37, -12.7) * mm, "end": v(1171.28, -12.7) * mm});
            skLineSegment(sketch, "E39.left", {"start": v(-600.37, 533.4) * mm, "end": v(-600.37, -12.7) * mm});
            skLineSegment(sketch, "E39.right", {"start": v(1171.28, 533.4) * mm, "end": v(1171.28, -12.7) * mm});
            skSolve(sketch);
        }
        {
            var Q0;
            Q0 = qSketchRegion(id + "F60", true);
            extrude(context, id + "F61", {"entities" : qUnion([Q0]), "oppositeDirection" : true, "depth" : 19.05 * mm});
        }
        {
            var Q0;
            Q0=makeQuery(id+"F29.opExtrude","SWEPT_FACE",FACE,{"disambiguationData":[OSD([sQuery(id+"F28.wireOp",EDGE,"E21.top")])]});
            var sketch = newSketch(context, id + "F62", { "sketchPlane" : qUnion([Q0])});
            skLineSegment(sketch, "E40.bottom", {"start": v(-600.37, 12.7) * mm, "end": v(1171.28, 12.7) * mm});
            skLineSegment(sketch, "E40.top", {"start": v(-600.37, -533.4) * mm, "end": v(1171.28, -533.4) * mm});
            skLineSegment(sketch, "E40.left", {"start": v(-600.37, 12.7) * mm, "end": v(-600.37, -533.4) * mm});
            skLineSegment(sketch, "E40.right", {"start": v(1171.28, 12.7) * mm, "end": v(1171.28, -533.4) * mm});
            skSolve(sketch);
        }
        {
            var Q0;
            Q0 = qSketchRegion(id + "F62", true);
            extrude(context, id + "F63", {"entities" : qUnion([Q0]), "oppositeDirection" : true, "depth" : 19.05 * mm});
        }
    });
